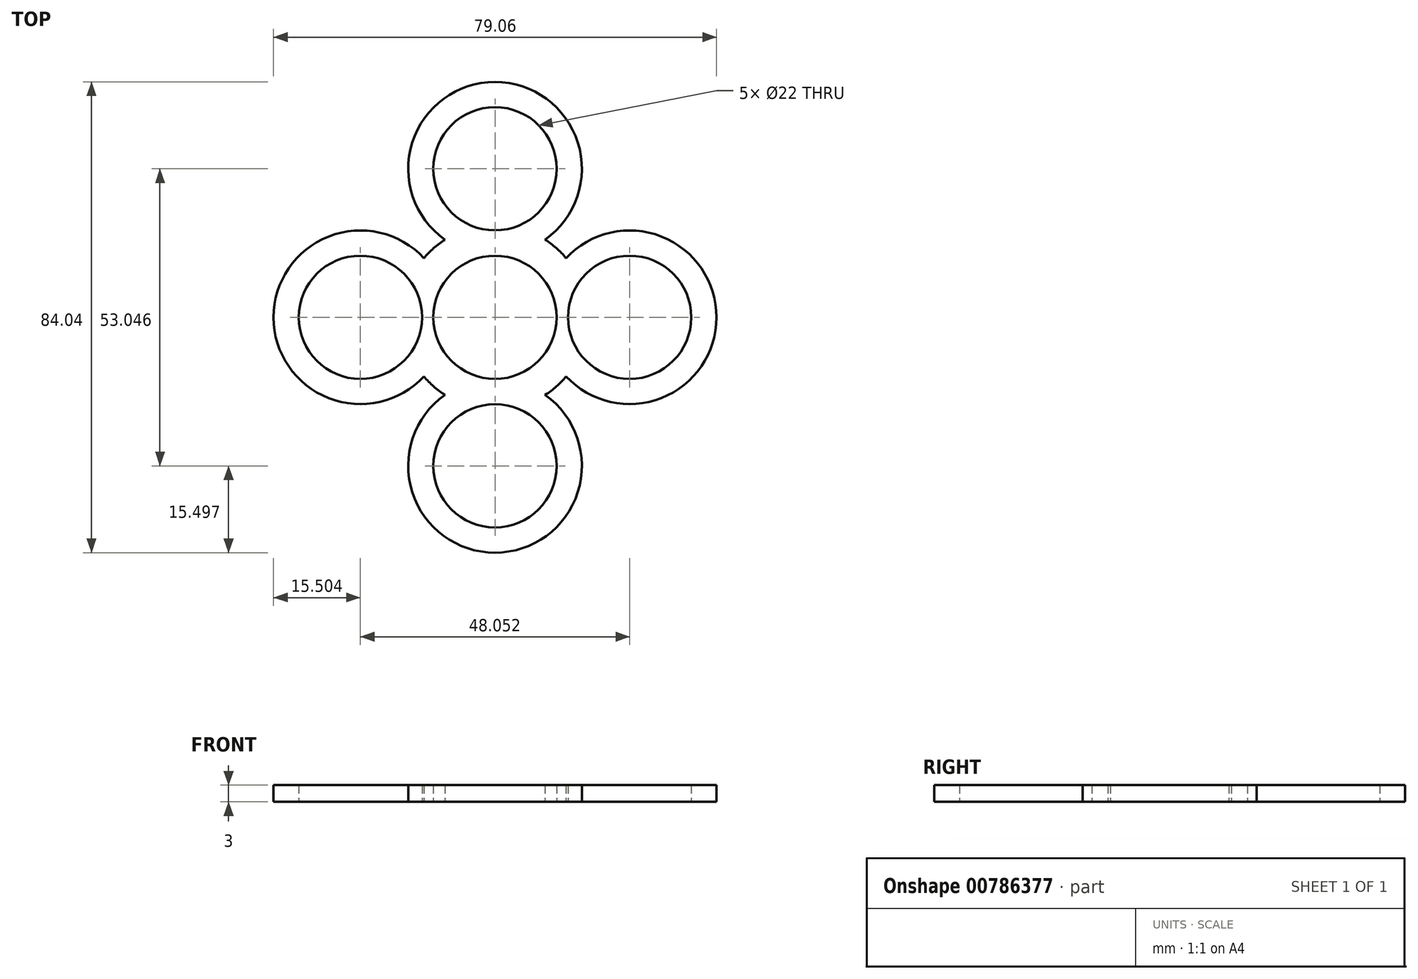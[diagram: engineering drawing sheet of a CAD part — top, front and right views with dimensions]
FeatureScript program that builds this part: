
annotation { "Feature Type Name" : "Feature", "Feature Type Description" : "" }
export const myFeature = defineFeature(function(context is Context, id is Id, definition is map)
    precondition{}
    {
        {
            var Q0;
            Q0=qCreatedBy(makeId("Top.planeOp"),FACE);
            var sketch = newSketch(context, id + "F0", { "sketchPlane" : qUnion([Q0])});
            skCircle(sketch, "E0", {"center": v(0, 0) * mm, "radius": 11 * mm});
            skArc(sketch, "E1", {"start": v(12.68, 10.56) * mm, "mid": v(10.94, 12.35) * mm, "end": v(8.95, 13.86) * mm});
            skCircle(sketch, "E2", {"center": v(0, 26.52) * mm, "radius": 11 * mm});
            skArc(sketch, "E3", {"start": v(8.95, 13.86) * mm, "mid": v(0, 42.02) * mm, "end": v(-8.95, 13.86) * mm});
            skArc(sketch, "E4.MirrorC", {"start": v(8.95, -13.86) * mm, "mid": v(0, -42.02) * mm, "end": v(-8.95, -13.86) * mm});
            skCircle(sketch, "E5", {"center": v(-24.03, 0) * mm, "radius": 11 * mm});
            skArc(sketch, "E6", {"start": v(-12.68, 10.56) * mm, "mid": v(-39.53, 0) * mm, "end": v(-12.68, -10.56) * mm});
            skArc(sketch, "E7.MirrorC", {"start": v(12.68, 10.56) * mm, "mid": v(39.53, 0) * mm, "end": v(12.68, -10.56) * mm});
            skCircle(sketch, "E8.MirrorC", {"center": v(24.03, 0) * mm, "radius": 11 * mm});
            skArc(sketch, "E9.trimOffspring", {"start": v(-8.95, 13.86) * mm, "mid": v(-10.94, 12.35) * mm, "end": v(-12.68, 10.56) * mm});
            skArc(sketch, "E10.trimOffspring", {"start": v(-12.68, -10.56) * mm, "mid": v(-10.94, -12.35) * mm, "end": v(-8.95, -13.86) * mm});
            skArc(sketch, "E11.trimOffspring", {"start": v(8.95, -13.86) * mm, "mid": v(10.94, -12.35) * mm, "end": v(12.68, -10.56) * mm});
            skCircle(sketch, "E12", {"center": v(0, -26.52) * mm, "radius": 11 * mm});
            skSolve(sketch);
        }
        {
            var Q0;
            Q0 = qSketchRegion(id + "F0", true);
            extrude(context, id + "F1", {"entities" : qUnion([Q0]), "depth" : 3 * mm, "offsetDistance" : 25 * mm});
        }
    });
